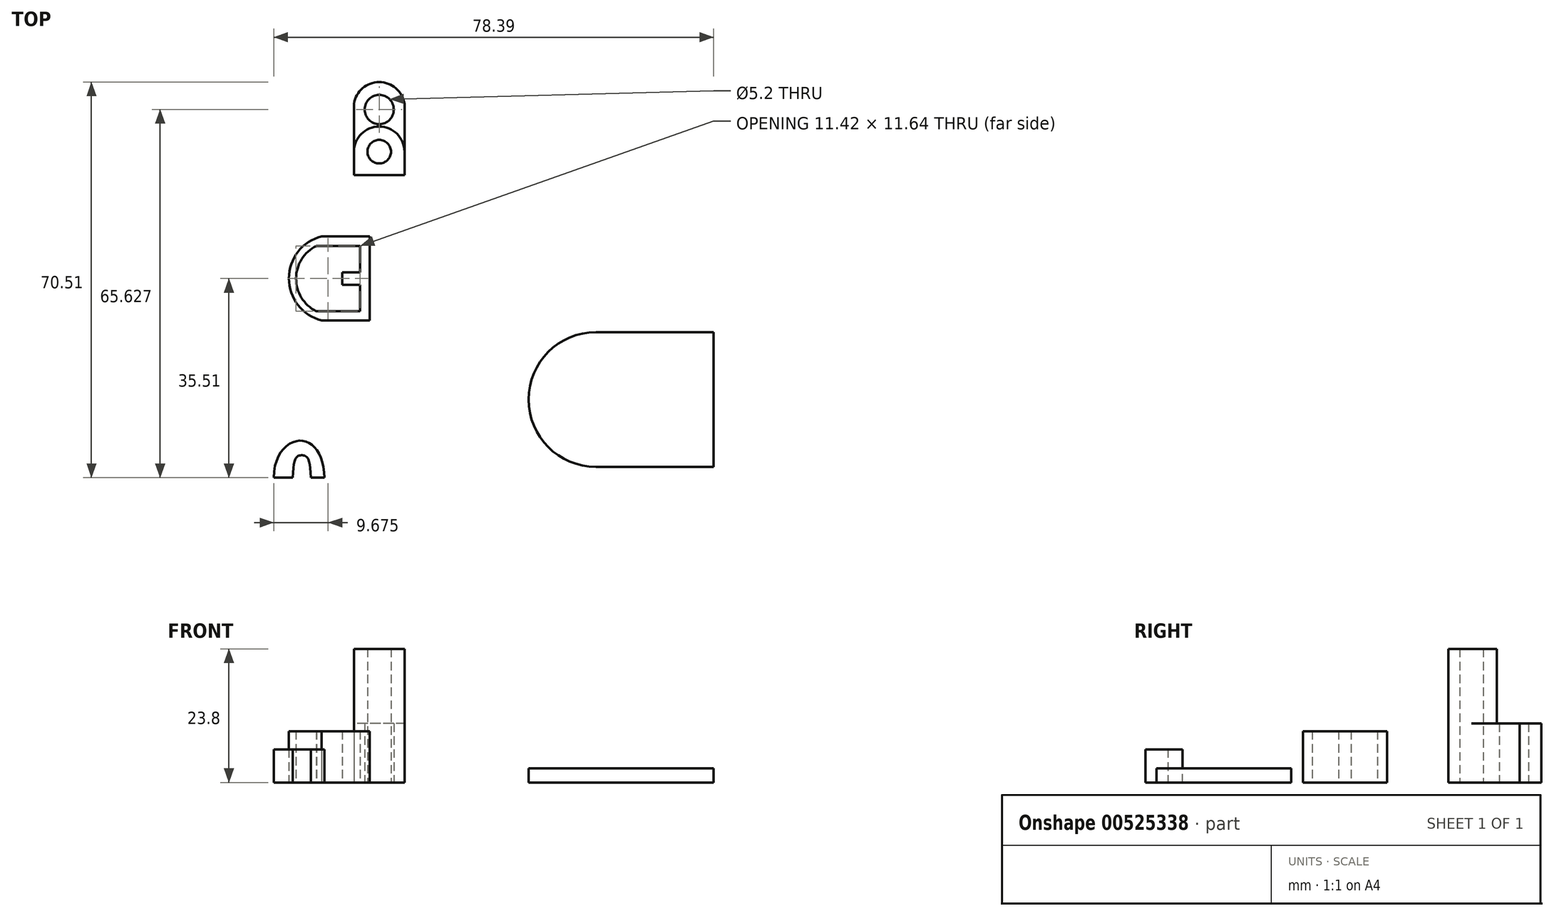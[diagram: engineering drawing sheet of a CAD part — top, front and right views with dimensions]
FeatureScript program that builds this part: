
annotation { "Feature Type Name" : "Feature", "Feature Type Description" : "" }
export const myFeature = defineFeature(function(context is Context, id is Id, definition is map)
    precondition{}
    {
        {
            var Q0;
            Q0=qCreatedBy(makeId("Top.planeOp"),FACE);
            var sketch = newSketch(context, id + "F0", { "sketchPlane" : qUnion([Q0])});
            skLineSegment(sketch, "E0.bottom", {"start": v(11.67, -0.88) * mm, "end": v(32.67, -0.88) * mm});
            skLineSegment(sketch, "E0.top", {"start": v(11.67, -24.88) * mm, "end": v(32.67, -24.88) * mm});
            skLineSegment(sketch, "E0.right", {"start": v(32.67, -0.88) * mm, "end": v(32.67, -24.88) * mm});
            skArc(sketch, "E1", {"start": v(11.67, -0.88) * mm, "mid": v(-0.33, -12.88) * mm, "end": v(11.67, -24.88) * mm});
            skSolve(sketch);
        }
        {
            var Q0;
            Q0=makeQuery(id+"F0.imprint","IMPRINT",FACE,{"disambiguationData":[TD([[makeQuery(id+"F0.imprint","IMPRINT",EDGE,{"derivedFrom":sQuery(id+"F0.wireOp",EDGE,"E0.bottom")}),-1.0]])]});
            extrude(context, id + "F1", {"entities" : qUnion([Q0]), "depth" : 2.5 * mm, "offsetDistance" : 25 * mm});
        }
        {
            var Q0;
            Q0=qCreatedBy(makeId("Top.planeOp"),FACE);
            var sketch = newSketch(context, id + "F2", { "sketchPlane" : qUnion([Q0])});
            skLineSegment(sketch, "E2.top", {"start": v(-31.33, 7.57) * mm, "end": v(-33.53, 7.57) * mm});
            skLineSegment(sketch, "E2.right", {"start": v(-33.53, 8.7) * mm, "end": v(-33.53, 7.57) * mm});
            skLineSegment(sketch, "E3.MirrorCS", {"start": v(-33.53, 8.7) * mm, "end": v(-33.53, 9.83) * mm});
            skLineSegment(sketch, "E4.MirrorCS", {"start": v(-31.33, 9.79) * mm, "end": v(-33.58, 9.79) * mm});
            skLineSegment(sketch, "E5.0", {"start": v(-37.18, 16.2) * mm, "end": v(-28.63, 16.2) * mm});
            skArc(sketch, "E5.1", {"start": v(-37.18, 16.2) * mm, "mid": v(-43.03, 8.7) * mm, "end": v(-37.18, 1.2) * mm});
            skLineSegment(sketch, "E5.2", {"start": v(-37.18, 1.2) * mm, "end": v(-28.63, 1.2) * mm});
            skLineSegment(sketch, "E5.3", {"start": v(-28.63, 16.2) * mm, "end": v(-28.63, 1.2) * mm});
            skLineSegment(sketch, "E6.3", {"start": v(-30.33, 14.5) * mm, "end": v(-30.33, 9.79) * mm});
            skLineSegment(sketch, "E6.4", {"start": v(-36.84, 14.5) * mm, "end": v(-30.33, 14.5) * mm});
            skLineSegment(sketch, "E6.6", {"start": v(-30.33, 7.57) * mm, "end": v(-30.33, 2.86) * mm});
            skLineSegment(sketch, "E6.7", {"start": v(-36.84, 2.86) * mm, "end": v(-30.33, 2.86) * mm});
            skLineSegment(sketch, "E6.8", {"start": v(-36.84, 2.86) * mm, "end": v(-38.18, 2.86) * mm});
            skArc(sketch, "E6.9", {"start": v(-38.1, 14.5) * mm, "mid": v(-41.76, 8.7) * mm, "end": v(-38.18, 2.86) * mm});
            skLineSegment(sketch, "E6.10", {"start": v(-36.84, 14.5) * mm, "end": v(-38.1, 14.5) * mm});
            skLineSegment(sketch, "E7", {"start": v(-30.33, 7.57) * mm, "end": v(-32.43, 7.57) * mm});
            skLineSegment(sketch, "E8", {"start": v(-31.33, 9.79) * mm, "end": v(-30.33, 9.79) * mm});
            skSolve(sketch);
        }
        {
            var Q0;
            {var subQ0=sQuery(id+"F2.wireOp",EDGE,"E2.top");Q0=makeQuery(id+"F2.imprint","IMPRINT",FACE,{"disambiguationData":[TD([[makeQuery(id+"F2.imprint","IMPRINT",EDGE,{"derivedFrom":subQ0}),-1.0]])]});}
            extrude(context, id + "F3", {"entities" : qUnion([Q0]), "depth" : 9.14 * mm, "offsetDistance" : 25 * mm});
        }
        {
            var Q0;
            Q0=qCreatedBy(makeId("Top.planeOp"),FACE);
            var sketch = newSketch(context, id + "F4", { "sketchPlane" : qUnion([Q0])});
            skLineSegment(sketch, "E9", {"start": v(-36.72, -26.83) * mm, "end": v(-39.12, -26.83) * mm});
            skLineSegment(sketch, "E10", {"start": v(-42.32, -26.83) * mm, "end": v(-45.72, -26.83) * mm});
            skPoint(sketch, "E11.endSnap0", {"position": v(-40.72, -26.83) * mm});
            skFitSpline(sketch, "E12", {"points": [v(-45.72, -26.83) * mm, v(-40.72, -20.23) * mm, v(-36.72, -26.83) * mm], "startDerivative": vector(0, 26.24) * mm, "endDerivative": vector(0.28, -23.62) * mm});
            skFitSpline(sketch, "E13", {"points": [v(-42.32, -26.83) * mm, v(-40.72, -22.83) * mm, v(-39.12, -26.83) * mm], "startDerivative": vector(0.05, 23.52) * mm, "endDerivative": vector(0.38, -23.4) * mm});
            skSolve(sketch);
        }
        {
            var Q0;
            Q0 = qSketchRegion(id + "F4", true);
            extrude(context, id + "F5", {"entities" : qUnion([Q0]), "depth" : 5.9 * mm, "offsetDistance" : 25 * mm});
        }
        {
            var Q0;
            Q0=makeQuery(id+"F5.opExtrude","SWEPT_BODY",BODY,{"disambiguationData":[OSD([sQuery(id+"F4.wireOp",EDGE,"E9"),sQuery(id+"F4.wireOp",EDGE,"E10"),sQuery(id+"F4.wireOp",EDGE,"E12"),sQuery(id+"F4.wireOp",EDGE,"E13")])]});
            transform(context, id + "F6", {"entities" : qUnion([Q0]), "transformType" : TransformType.TRANSLATION_3D, "dx" : 0 * mm, "dy" : 0 * mm, "dz" : 0 * mm, "makeCopy" : true});
        }
        {
            var Q0;
            Q0=qCreatedBy(makeId("Top.planeOp"),FACE);
            var sketch = newSketch(context, id + "F7", { "sketchPlane" : qUnion([Q0])});
            skLineSegment(sketch, "E14.top", {"start": v(-31.44, 27.13) * mm, "end": v(-22.44, 27.13) * mm});
            skLineSegment(sketch, "E14.left", {"start": v(-31.44, 39.83) * mm, "end": v(-31.44, 27.13) * mm});
            skLineSegment(sketch, "E14.right", {"start": v(-22.44, 39.83) * mm, "end": v(-22.44, 27.13) * mm});
            skArc(sketch, "E15", {"start": v(-25.2, 27.13) * mm, "mid": v(-26.94, 35.78) * mm, "end": v(-28.68, 27.13) * mm});
            skCircle(sketch, "E16", {"center": v(-26.94, 31.28) * mm, "radius": 2.1 * mm});
            skCircle(sketch, "E17", {"center": v(-26.94, 38.8) * mm, "radius": 2.6 * mm});
            skArc(sketch, "E18", {"start": v(-22.44, 39.83) * mm, "mid": v(-26.94, 43.68) * mm, "end": v(-31.44, 39.83) * mm});
            skSolve(sketch);
        }
        {
            var Q0;
            Q0=makeQuery(id+"F7.imprint","IMPRINT",FACE,{"disambiguationData":[TD([[makeQuery(id+"F7.imprint","IMPRINT",EDGE,{"derivedFrom":sQuery(id+"F7.wireOp",EDGE,"E16")}),-1.0]])]});
            var Q1;
            {var subQ0=sQuery(id+"F7.wireOp",EDGE,"E14.left");var subQ1=sQuery(id+"F7.wireOp",EDGE,"E14.top");var subQ2=makeQuery(id+"F7.imprint","INTERSECT",VERTEX,{"derivedFrom":[subQ1,subQ0]});Q1=makeQuery(id+"F7.imprint","IMPRINT",FACE,{"disambiguationData":[TD([[makeQuery(id+"F7.imprint","IMPRINT",EDGE,{"disambiguationData":[TD([[subQ2,-1.0]])],"derivedFrom":subQ1}),1.0]])]});}
            var Q2;
            {var subQ0=sQuery(id+"F7.wireOp",EDGE,"E14.right");var subQ1=sQuery(id+"F7.wireOp",EDGE,"E14.top");var subQ2=makeQuery(id+"F7.imprint","INTERSECT",VERTEX,{"derivedFrom":[subQ1,subQ0]});Q2=makeQuery(id+"F7.imprint","IMPRINT",FACE,{"disambiguationData":[TD([[makeQuery(id+"F7.imprint","IMPRINT",EDGE,{"disambiguationData":[TD([[subQ2,1.0]])],"derivedFrom":subQ1}),1.0]])]});}
            extrude(context, id + "F8", {"entities" : qUnion([Q0, Q1, Q2]), "depth" : 23.8 * mm, "offsetDistance" : 25 * mm});
        }
        {
            var Q0;
            {var subQ5=sQuery(id+"F7.wireOp",EDGE,"6ajBd7Xf-gG7t-XD08-brPc-W33lVvYvw5Qm");Q0=makeQuery(id+"F7.imprint","IMPRINT",FACE,{"disambiguationData":[TD([[makeQuery(id+"F7.imprint","IMPRINT",EDGE,{"derivedFrom":subQ5}),1.0]])]});}
            var Q1;
            Q1=makeQuery(id+"F7.imprint","IMPRINT",FACE,{"disambiguationData":[TD([[makeQuery(id+"F7.imprint","IMPRINT",EDGE,{"derivedFrom":sQuery(id+"F7.wireOp",EDGE,"E17")}),-1.0]])]});
            extrude(context, id + "F9", {"entities" : qUnion([Q0, Q1]), "operationType" : NewBodyOperationType.ADD, "depth" : 10.5 * mm, "offsetDistance" : 25 * mm});
        }
    });
